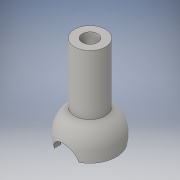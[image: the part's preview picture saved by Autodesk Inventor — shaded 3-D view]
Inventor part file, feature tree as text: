
AUTODESK INVENTOR PART (.ipt)
format: ipt  version: 2016 (Build 200138000, 138)  size: 162,304 bytes
history: native  units: in
note: dims shown in document units (in); Inventor stores cm internally (conversion verified against a paired STEP export)
features: sketch x10, plane x6, extrude x3, revolve x3, loft x2
ambient origin geometry x8: Origin, YZ Plane, XZ Plane, XY Plane, X Axis, Y Axis, Z Axis, Center Point
bodies: Body1 (feature_tree)
feature tree (24):
  sketch  "Sketch1"  dims[d0=0.5in d6=3.0in d7=0.0in]
  extrude  "Extrusion2"  Depth=3.0in TaperAngle=0.0deg
  plane  "Work Plane1"
  sketch  "Sketch9"  dims[d11=-0.125in d22=0.25in]
  plane  "Work Plane2"
  loft  "Loft1"
  sketch  "Sketch11"  dims[d25=0.0in d26=90.0deg d27=0.0in d28=90.0deg]
  revolve  "Revolution8"  [1 undecoded]
  revolve  "Revolution9"  Angle=90.0deg
  plane  "Work Plane4"
  revolve  "Revolution10"  Angle=90.0deg
  extrude  "Extrusion7"  [1 undecoded]
  plane  "Work Plane8"
  extrude  "Extrusion8"  Depth=1.0in TaperAngle=0.0deg
  sketch  "Sketch19"  dims[d51=0.25in]
  plane  "Work Plane9"
  loft  "Loft2"
  sketch  "Sketch10"  dims[d23=-0.185in d24=0.23in]
  sketch  "Sketch15"  dims[d29=0.72in d39=90.0deg]
  sketch  "Sketch16"  dims[d40=90.0deg d41=-2.9375in]
  sketch  "Sketch17"  dims[d42=180.0deg d43=1.0in d44=0.0in]
  plane  "Work Plane7"
  sketch  "Sketch18"  dims[d47=-0.1225in d48=1.462in d49=2.0in d50=0.0in]
  sketch  "Sketch20"  dims[d52=-0.185in d53=0.23in d54=0.0in d55=90.0deg d56=0.0in d57=90.0deg]
note: 2 required parameter values undecoded (feature->parameter linkage not recoverable at this tier; creation-order binding heuristic only, values carry confidence <= 0.55)